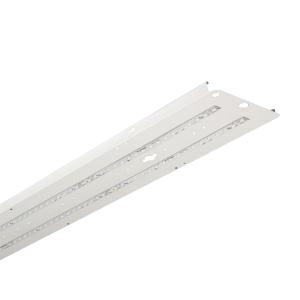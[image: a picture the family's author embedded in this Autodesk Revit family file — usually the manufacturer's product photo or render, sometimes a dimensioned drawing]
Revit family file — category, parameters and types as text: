
# Revit family: 3f_filippi_-_kit_led_retrofit_per_schermo_in_vetro_3f_filippi_-_a5118_a5184_-_kit_led_i3f_76__a3f_91__a3_9dea86ab9b8b432c
name_source: partatom
category: Lighting Fixtures
units: mm (PartAtom-declared; Revit-internal decimal feet)

## family parameters
Cut with Voids When Loaded = No
Host = Face
Light Source = No
Part Type = Normal
Room Calculation Point = No
Round Connector Dimension = Use Diameter
Shared = No

## types (1)
- 3F Filippi - Kit LED Retrofit per schermo in vetro (1 x LED, 6261 lm, 49 W, 4000 K)
    Apparent Load = 49 VA
    Approval mark = ENEC
    CIE Flux Codes = 62 90 98 100 100
    Color Rendering = 80
    Color Temperature = 4000 K
    Control Gear = Electronic ballast
    Default Elevation = 1800 mm
    Description = Led retrofit kit suitable for Fluorescent Beta 2x i3F 76, A3F 91 and A3F 93 luminaires.

ILLUMINOTECHNICAL
Luminous efficiency 100% (DLOR 100%, ULOR 0%).
Initial luminous flux of the luminaire 6261 lm.
Symmetric distribution.
Installation Interdistance Transv.D = 1.31 x hu - Long.D = 1.31 x hu.
Tabular UGR (CIE 117 - 4H-8H; S=0.25H; 70/50/20): RUG 18.6 - 19.9.
Beam angle: 90° - 99°.
Luminous efficacy 128 lm/W.
Lifetime (L93/B10): 30000 h. (tq+25°C)
Lifetime (L90/B10): 50000 h. (tq+25°C)
Lifetime (L85/B10): 80000 h. (tq+25°C)
Lifetime (L80/B10): 100000 h. (tq+25°C)
Lifetime (L85/B10): 50000 h. (tq+35°C)
Sudden decreased luminous flux after 50000 hours: 0% (C0).
Photobiological safety in compliance with IEC/TR 62778: RG0 risk exempt, (IEC 62471).
In compliance with IEC/EN 62722-2-1 - IEC/EN 62717 standards.

SOURCE
2 linear LED modules 22W/840.
Energy efficiency class (UE 2019/2020 - UE 2019/2015): D.
CIE 13.3 Colour rendering index: CRI >80 (R9 <50%).
IES TM-30 Fidelity Index: Rf = 84 Rg = 95.
CCT nominal colour temperature 4000 K.
Colour initial tolerance (MacAdam): SDCM 3.

MECHANICAL
Gear-tray unit in hot-galvanised steel, painted in white polyester, fixed to the housing by means of "Ribloc" rapid devices in galvanised steel, hinged opening.
Luminaire with limited surface temperature. - D - (EN 60598-2-24)
Dimensions: 1565x235 mm, height 135 mm. Weight 6.267 kg.
Glow-wire test resistance 850°C.

ELECTRICAL
Halogen Free electronic wiring 230V-50/60Hz, power factor 0.97, THD <25%, constant output current, SELV, class I, 1 driver.
Power of the luminaire 49 W.
CE - IEC 60598-1 - EN 60598-1.
SAFE FLICKER: PstLM=<1 and SVM=<0.4 (IEC TR 61547-1 and IEC TR 63158), to ensure a more comfortable and safe light.
Luminaire compliant with EN 60598-2-22 for power supply from a centralised emergency system CPSS (Central Power Supply System), not incorporated in the luminaire - high risk areas excluded. The default power and flux are 100% in AC and 100% in DC.
Ambient temperature from -20°C to +35°C.
Temperature class T6 max 85°C.
Relative humidity UR: <85%.

INSTALLATION
Retrofit.
Correct installation of the retrofit LED kit, compliant with EN 60598-1 and CE marked, inside the 3F Filippi - Beta 2x i3F 76, A3F 91 and A3F 93 Fluorescent luminaires must be only carried out by qualified personnel to ensure compliance with the national installation standards.
Attention: to maintain the degree of protection of the device and for the purposes of validity of the guarantee of the new retrofit kits, it is imperative to replace the old cable guides (on the body of the device) with the new ones supplied.
All accessories dedicated to this product are available on the Catalog and on our website www.3F-Filippi.com.

ACCESSORIES
A5184 - Printed glass Beta 2x i3F 76 - L1565.

WARNING
Fixture not suitable for cold stores with an ambient temperature <0°C and/or relative humidity >85%.
Luminaire designed for disposal/recycling at end-of-life.
Replaceable (LED only) light source by a professional. Replaceable control gear by a professional.
    Height = 135 mm
    Lamp = 1 x LED
    Lamp Light Flux = 6261 lm
    Lamp Power = 49 W
    Lamp count = 1
    Length = 1565 mm
    Lifetime = 50000 h
    Luminous efficacy = 128 lm/W
    Manufacturer = 3F Filippi
    ModVariant = No
    Model = 3F Filippi - A5118+A5184 - Kit LED I3F 76, A3F 91, A3F 93 - L1565-2X22W + VS
    Mounting Place = Ceiling
    Mounting Type = Surface mounted
    Number of Poles = 1
    OnlyDefault = Yes
    Power Factor = 1
    Product Name = 3F Filippi - Kit LED Retrofit per schermo in vetro
    Product group = ceiling mounted luminaire
    ProductGroupID = 3
    Protection Class = Protection class I
    Protection Degree = Degree of protection
    RLX_Detail_Level = 1
    RLX_Emergency_Light_Flux = 0 lm
    RLX_Emergency_Type = 0
    RLX_Emergency_Type_DB = No
    RlxData = <blob elided: 53177 chars, md5=ab2b2f2e>
    Socket = socket
    Standby Power = 0 W
    System Light Flux = 6261 lm
    System Power = 49 W
    Type Comments = Product without accessories
    Type Image = 3ffilippi_a5118_a5184.jpg
    URL = http://relux.com
    VarID = ---
    Voltage = 0 V
    Weight = 0.00 kg
    Width = 235 mm

## geometry (parser evidence)
native form markers: Blend x4, Sweep x12
no freeform markers — native parametric forms only
